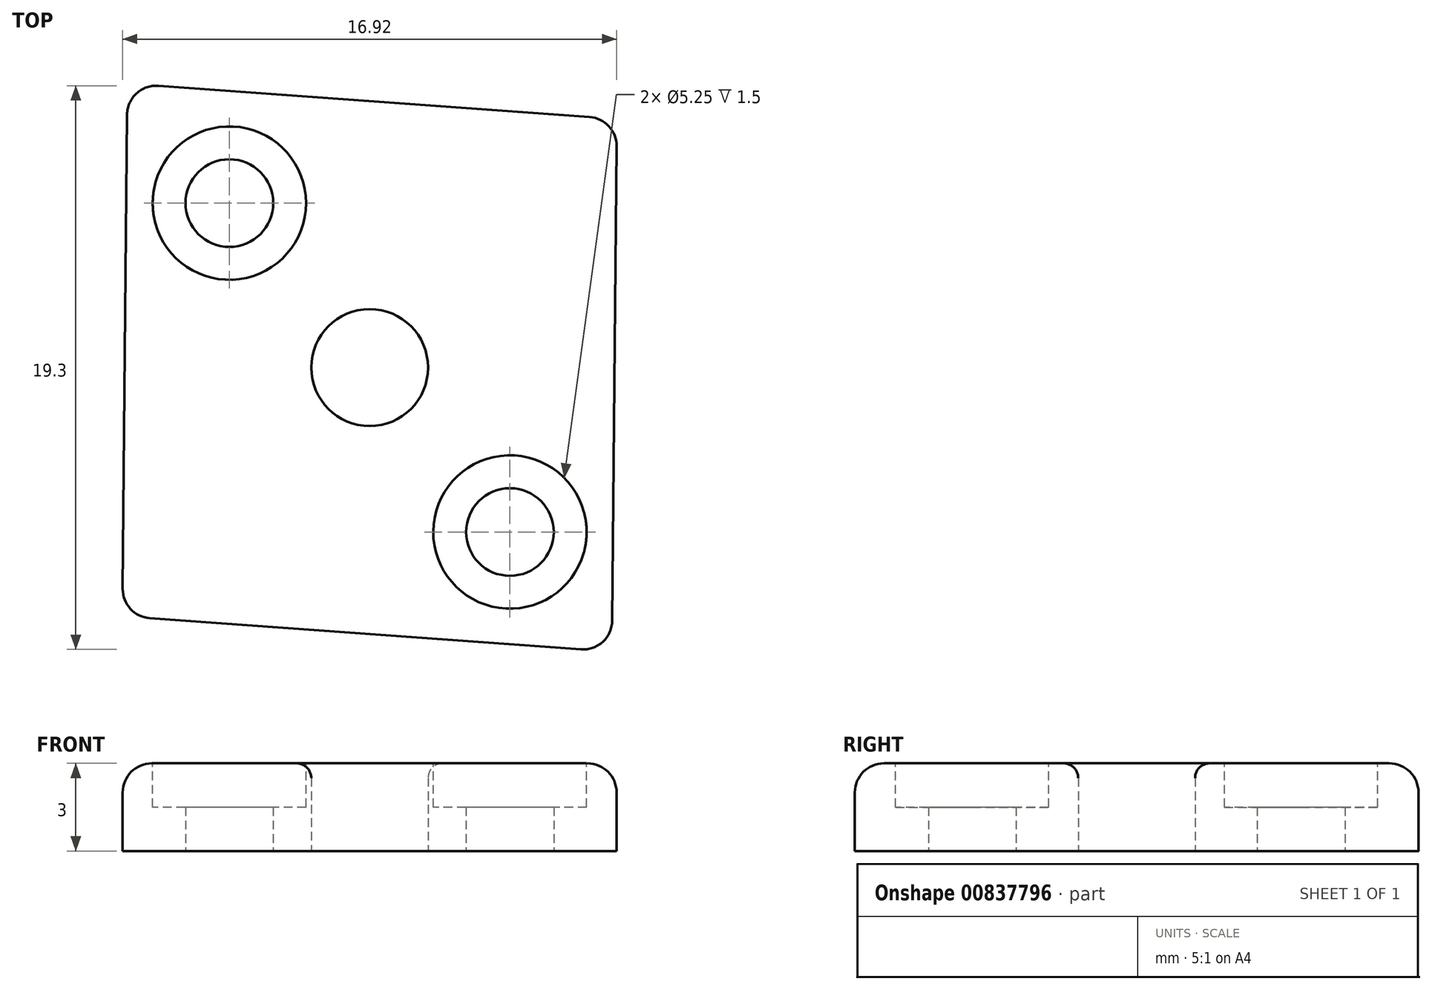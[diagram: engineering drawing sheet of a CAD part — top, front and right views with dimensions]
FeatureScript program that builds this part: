
annotation { "Feature Type Name" : "Feature", "Feature Type Description" : "" }
export const myFeature = defineFeature(function(context is Context, id is Id, definition is map)
    precondition{}
    {
        {
            var Q0;
            Q0=qCreatedBy(makeId("Top.planeOp"),FACE);
            var sketch = newSketch(context, id + "F0", { "sketchPlane" : qUnion([Q0])});
            skLineSegment(sketch, "E0", {"start": v(-6.35, 0.53) * mm, "end": v(6.35, -0.53) * mm, "construction": true});
            skLineSegment(sketch, "E1", {"start": v(0, -6.91) * mm, "end": v(0, 6.91) * mm, "construction": true});
            skCircle(sketch, "E2", {"center": v(0, 0) * mm, "radius": 2 * mm});
            skLineSegment(sketch, "E3", {"start": v(0, 0) * mm, "end": v(-0.85, 1.8) * mm, "construction": true});
            skLineSegment(sketch, "E4", {"start": v(0, 0) * mm, "end": v(-1.14, -1.64) * mm, "construction": true});
            skLineSegment(sketch, "E5", {"start": v(0, 0) * mm, "end": v(1.14, 1.64) * mm, "construction": true});
            skLineSegment(sketch, "E6", {"start": v(0, 0) * mm, "end": v(0.85, -1.8) * mm, "construction": true});
            skLineSegment(sketch, "E7", {"start": v(1.14, 1.64) * mm, "end": v(2.3, 3.32) * mm, "construction": true});
            skLineSegment(sketch, "E8", {"start": v(2, -0.17) * mm, "end": v(4.03, -0.34) * mm, "construction": true});
            skLineSegment(sketch, "E9", {"start": v(-2, 0.17) * mm, "end": v(-4.03, 0.34) * mm, "construction": true});
            skLineSegment(sketch, "E10", {"start": v(-1.14, -1.64) * mm, "end": v(-2.3, -3.32) * mm, "construction": true});
            skLineSegment(sketch, "E11", {"start": v(0.85, -1.8) * mm, "end": v(1.72, -3.66) * mm, "construction": true});
            skLineSegment(sketch, "E12", {"start": v(-0.85, 1.8) * mm, "end": v(-1.72, 3.66) * mm, "construction": true});
            skLineSegment(sketch, "E13", {"start": v(-4.03, 0.34) * mm, "end": v(-1.72, 3.66) * mm});
            skLineSegment(sketch, "E14", {"start": v(-1.72, 3.66) * mm, "end": v(2.3, 3.32) * mm});
            skLineSegment(sketch, "E15", {"start": v(2.3, 3.32) * mm, "end": v(4.03, -0.34) * mm});
            skLineSegment(sketch, "E16", {"start": v(4.03, -0.34) * mm, "end": v(1.72, -3.66) * mm});
            skLineSegment(sketch, "E17", {"start": v(1.72, -3.66) * mm, "end": v(-2.3, -3.32) * mm});
            skLineSegment(sketch, "E18", {"start": v(-2.3, -3.32) * mm, "end": v(-4.03, 0.34) * mm});
            skLineSegment(sketch, "E19", {"start": v(0, 0) * mm, "end": v(-6.35, 7.44) * mm, "construction": true});
            skLineSegment(sketch, "E20", {"start": v(-6.35, 7.44) * mm, "end": v(-8.3, 9.73) * mm, "construction": true});
            skLineSegment(sketch, "E21", {"start": v(0, 0) * mm, "end": v(6.35, 6.39) * mm, "construction": true});
            skLineSegment(sketch, "E22", {"start": v(6.35, 6.39) * mm, "end": v(8.46, 8.51) * mm, "construction": true});
            skLineSegment(sketch, "E23", {"start": v(0, 0) * mm, "end": v(6.35, -7.44) * mm, "construction": true});
            skLineSegment(sketch, "E24", {"start": v(6.35, -7.44) * mm, "end": v(8.3, -9.73) * mm, "construction": true});
            skLineSegment(sketch, "E25", {"start": v(0, 0) * mm, "end": v(-6.35, -6.39) * mm, "construction": true});
            skLineSegment(sketch, "E26", {"start": v(-6.35, -6.39) * mm, "end": v(-8.46, -8.51) * mm, "construction": true});
            skLineSegment(sketch, "E27", {"start": v(-8.3, 9.73) * mm, "end": v(-8.46, -8.51) * mm});
            skLineSegment(sketch, "E28", {"start": v(-8.46, -8.51) * mm, "end": v(8.3, -9.73) * mm});
            skLineSegment(sketch, "E29", {"start": v(8.3, -9.73) * mm, "end": v(8.46, 8.51) * mm});
            skLineSegment(sketch, "E30", {"start": v(8.46, 8.51) * mm, "end": v(-8.3, 9.73) * mm});
            skLineSegment(sketch, "E31", {"start": v(-8.3, 9.73) * mm, "end": v(-2.35, 2.75) * mm, "construction": true});
            skLineSegment(sketch, "E32", {"start": v(8.46, 8.51) * mm, "end": v(2.62, 2.64) * mm, "construction": true});
            skLineSegment(sketch, "E33", {"start": v(8.3, -9.73) * mm, "end": v(2.35, -2.75) * mm, "construction": true});
            skLineSegment(sketch, "E34", {"start": v(-8.46, -8.51) * mm, "end": v(-2.62, -2.64) * mm, "construction": true});
            skLineSegment(sketch, "E35", {"start": v(-5.32, 6.24) * mm, "end": v(-5, 5.86) * mm, "construction": true});
            skLineSegment(sketch, "E36", {"start": v(5.32, -6.24) * mm, "end": v(5, -5.86) * mm, "construction": true});
            skLineSegment(sketch, "E37", {"start": v(5.32, -6.24) * mm, "end": v(4.8, -5.63) * mm, "construction": true});
            skCircle(sketch, "E38", {"center": v(4.8, -5.63) * mm, "radius": 1.5 * mm});
            skLineSegment(sketch, "E39", {"start": v(-5.32, 6.24) * mm, "end": v(-4.8, 5.63) * mm, "construction": true});
            skCircle(sketch, "E40", {"center": v(-4.8, 5.63) * mm, "radius": 1.5 * mm});
            skCircle(sketch, "E41", {"center": v(-4.8, 5.63) * mm, "radius": 2.62 * mm});
            skCircle(sketch, "E42", {"center": v(4.8, -5.63) * mm, "radius": 2.62 * mm});
            skSolve(sketch);
        }
        {
            var Q0;
            Q0=makeQuery(id+"F0.imprint","IMPRINT",FACE,{"disambiguationData":[TD([[makeQuery(id+"F0.imprint","IMPRINT",EDGE,{"derivedFrom":sQuery(id+"F0.wireOp",EDGE,"E13")}),1.0]])]});
            var Q1;
            Q1=makeQuery(id+"F0.imprint","IMPRINT",FACE,{"disambiguationData":[TD([[makeQuery(id+"F0.imprint","IMPRINT",EDGE,{"derivedFrom":sQuery(id+"F0.wireOp",EDGE,"E2")}),-1.0]])]});
            var Q2;
            Q2=makeQuery(id+"F0.imprint","IMPRINT",FACE,{"disambiguationData":[TD([[makeQuery(id+"F0.imprint","IMPRINT",EDGE,{"derivedFrom":sQuery(id+"F0.wireOp",EDGE,"E40")}),-1.0]])]});
            var Q3;
            Q3=makeQuery(id+"F0.imprint","IMPRINT",FACE,{"disambiguationData":[TD([[makeQuery(id+"F0.imprint","IMPRINT",EDGE,{"derivedFrom":sQuery(id+"F0.wireOp",EDGE,"E38")}),-1.0]])]});
            extrude(context, id + "F1", {"entities" : qUnion([Q0, Q1, Q2, Q3]), "depth" : 3 * mm, "offsetDistance" : 25 * mm});
        }
        {
            var Q0;
            Q0=makeQuery(id+"F1.opExtrude","CAP_FACE",FACE,{"disambiguationData":[OSD([sQuery(id+"F0.wireOp",EDGE,"E2"),sQuery(id+"F0.wireOp",EDGE,"E27"),sQuery(id+"F0.wireOp",EDGE,"E28"),sQuery(id+"F0.wireOp",EDGE,"E29"),sQuery(id+"F0.wireOp",EDGE,"E30"),sQuery(id+"F0.wireOp",EDGE,"E38"),sQuery(id+"F0.wireOp",EDGE,"E40")])],"isStart":false});
            var sketch = newSketch(context, id + "F2", { "sketchPlane" : qUnion([Q0])});
            skCircle(sketch, "E43", {"center": v(-4.8, 5.63) * mm, "radius": 2.62 * mm});
            skCircle(sketch, "E44", {"center": v(4.8, -5.63) * mm, "radius": 2.62 * mm});
            skSolve(sketch);
        }
        {
            var Q0;
            Q0=makeQuery(id+"F2.imprint","IMPRINT",FACE,{"disambiguationData":[TD([[makeQuery(id+"F2.imprint","IMPRINT",EDGE,{"derivedFrom":sQuery(id+"F2.wireOp",EDGE,"E43")}),1.0]])]});
            var Q1;
            Q1=makeQuery(id+"F2.imprint","IMPRINT",FACE,{"disambiguationData":[TD([[makeQuery(id+"F2.imprint","IMPRINT",EDGE,{"derivedFrom":sQuery(id+"F2.wireOp",EDGE,"E44")}),1.0]])]});
            extrude(context, id + "F3", {"entities" : qUnion([Q0, Q1]), "operationType" : NewBodyOperationType.REMOVE, "oppositeDirection" : true, "depth" : 1.5 * mm, "offsetDistance" : 25 * mm});
        }
        {
            var Q0;
            Q0=makeQuery(id+"F1.opExtrude","CAP_EDGE",EDGE,{"disambiguationData":[OSD([sQuery(id+"F0.wireOp",EDGE,"E27")])],"isStart":false});
            var Q1;
            Q1=makeQuery(id+"F1.opExtrude","CAP_EDGE",EDGE,{"disambiguationData":[OSD([sQuery(id+"F0.wireOp",EDGE,"E30")])],"isStart":false});
            var Q2;
            Q2=makeQuery(id+"F1.opExtrude","CAP_EDGE",EDGE,{"disambiguationData":[OSD([sQuery(id+"F0.wireOp",EDGE,"E29")])],"isStart":false});
            var Q3;
            Q3=makeQuery(id+"F1.opExtrude","CAP_EDGE",EDGE,{"disambiguationData":[OSD([sQuery(id+"F0.wireOp",EDGE,"E28")])],"isStart":false});
            var Q4;
            Q4=makeQuery(id+"F1.opExtrude","SWEPT_EDGE",EDGE,{"disambiguationData":[OSD([sQuery(id+"F0.wireOp",EDGE,"E29"),sQuery(id+"F0.wireOp",EDGE,"E30")])]});
            var Q5;
            Q5=makeQuery(id+"F1.opExtrude","SWEPT_EDGE",EDGE,{"disambiguationData":[OSD([sQuery(id+"F0.wireOp",EDGE,"E28"),sQuery(id+"F0.wireOp",EDGE,"E29")])]});
            var Q6;
            Q6=makeQuery(id+"F1.opExtrude","SWEPT_EDGE",EDGE,{"disambiguationData":[OSD([sQuery(id+"F0.wireOp",EDGE,"E27"),sQuery(id+"F0.wireOp",EDGE,"E30")])]});
            var Q7;
            Q7=makeQuery(id+"F1.opExtrude","SWEPT_EDGE",EDGE,{"disambiguationData":[OSD([sQuery(id+"F0.wireOp",EDGE,"E27"),sQuery(id+"F0.wireOp",EDGE,"E28")])]});
            fillet(context, id + "F4", {"entities" : qUnion([Q0, Q1, Q2, Q3, Q4, Q5, Q6, Q7]), "radius" : 1 * mm, "tangentPropagation" : true, "allowEdgeOverflow" : false});
        }
        {
            var Q0;
            Q0=makeQuery(id+"F1.opExtrude","CAP_EDGE",EDGE,{"disambiguationData":[OSD([sQuery(id+"F0.wireOp",EDGE,"E2")])],"isStart":false});
            fillet(context, id + "F5", {"entities" : qUnion([Q0]), "radius" : .5 * mm, "tangentPropagation" : true, "allowEdgeOverflow" : false});
        }
    });
